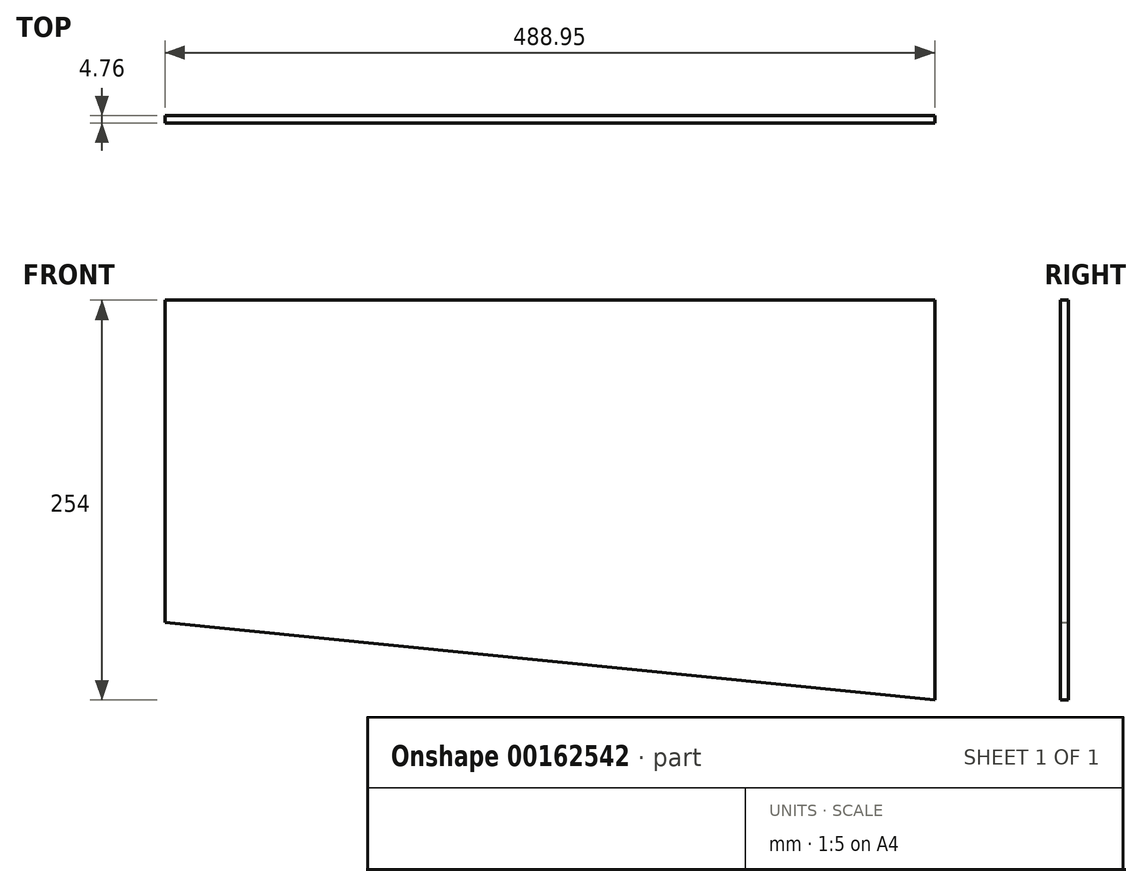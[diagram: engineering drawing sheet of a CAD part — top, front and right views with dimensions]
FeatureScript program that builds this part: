
annotation { "Feature Type Name" : "Feature", "Feature Type Description" : "" }
export const myFeature = defineFeature(function(context is Context, id is Id, definition is map)
    precondition{}
    {
        {
            var Q0;
            Q0=qCreatedBy(makeId("Front.planeOp"),FACE);
            var sketch = newSketch(context, id + "F0", { "sketchPlane" : qUnion([Q0])});
            skLineSegment(sketch, "E0.top", {"start": v(0, 254) * mm, "end": v(-473.08, 254) * mm});
            skLineSegment(sketch, "E0.left", {"start": v(0, 0) * mm, "end": v(0, 254) * mm});
            skLineSegment(sketch, "E1", {"start": v(-473.08, 254) * mm, "end": v(-504.83, 254) * mm});
            skLineSegment(sketch, "E2", {"start": v(-504.83, 50.8) * mm, "end": v(0, 0) * mm});
            skLineSegment(sketch, "E3", {"start": v(-488.95, 254) * mm, "end": v(-488.95, 49.2) * mm});
            skSolve(sketch);
        }
        {
            var Q0;
            Q0=qSketchRegion(id+"F0",true);
            extrude(context, id + "F1", {"entities" : qUnion([Q0]), "depth" : 4.76 * mm});
        }
    });
